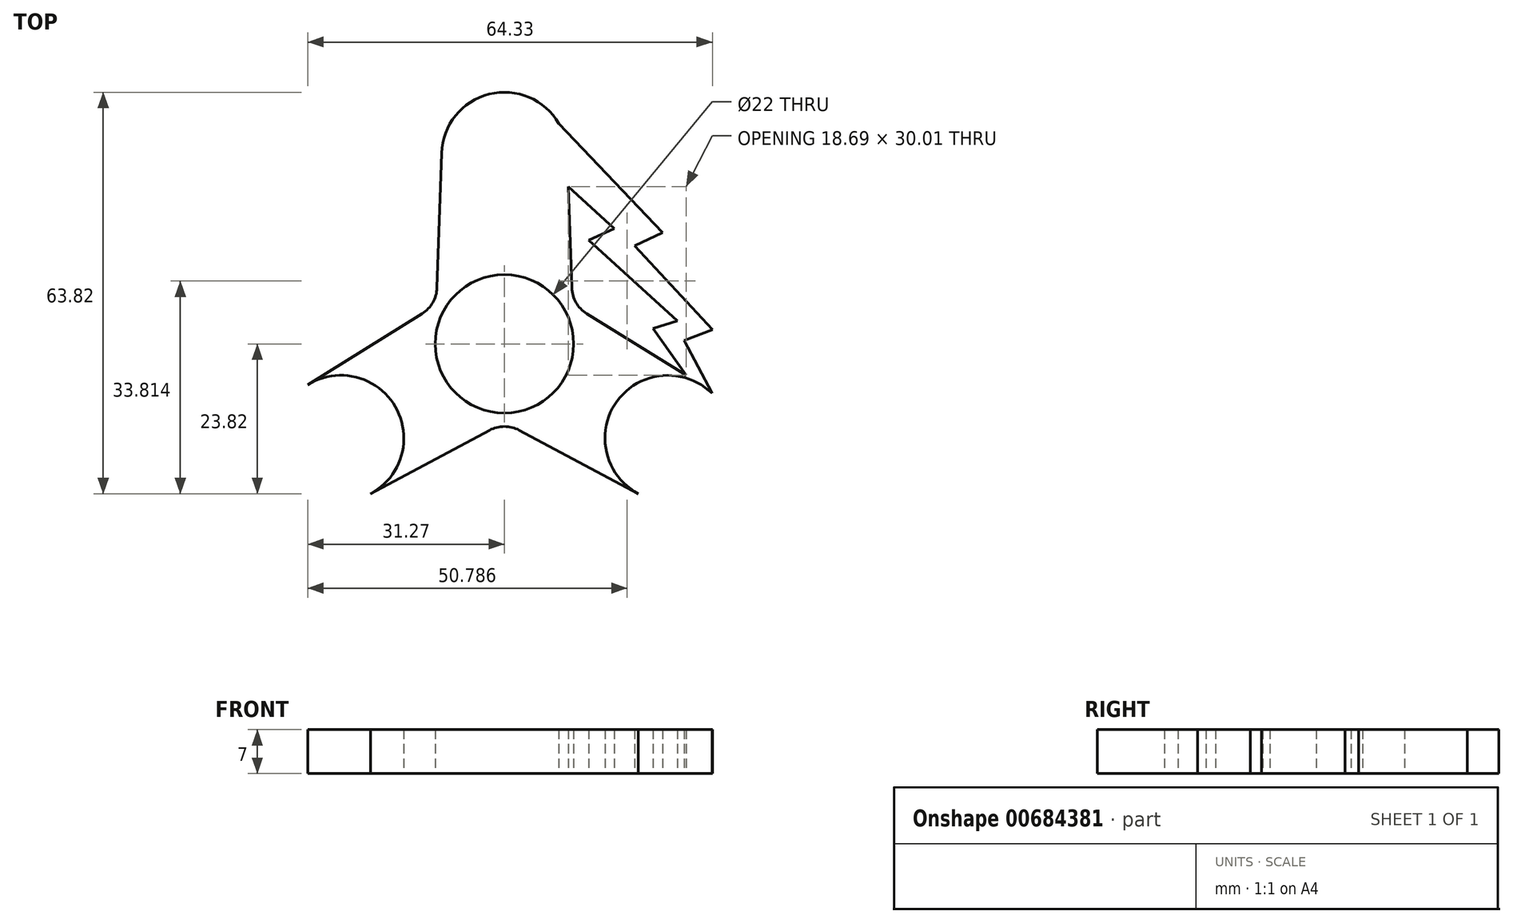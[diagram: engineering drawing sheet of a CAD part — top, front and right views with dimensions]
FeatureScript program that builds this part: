
annotation { "Feature Type Name" : "Feature", "Feature Type Description" : "" }
export const myFeature = defineFeature(function(context is Context, id is Id, definition is map)
    precondition{}
    {
        {
            var Q0;
            Q0=qCreatedBy(makeId("Top.planeOp"),FACE);
            var sketch = newSketch(context, id + "F0", { "sketchPlane" : qUnion([Q0])});
            skCircle(sketch, "E0", {"center": v(0, 0) * mm, "radius": 11 * mm});
            skLineSegment(sketch, "E1", {"start": v(-51.96, 30) * mm, "end": v(51.96, -30) * mm, "construction": true});
            skLineSegment(sketch, "E2.MirrorCS", {"start": v(51.96, 30) * mm, "end": v(-51.96, -30) * mm, "construction": true});
            skCircle(sketch, "E3", {"center": v(0, 30) * mm, "radius": 10 * mm});
            skCircle(sketch, "E4.MirrorC", {"center": v(-25.98, -15) * mm, "radius": 10 * mm});
            skCircle(sketch, "E5.MirrorC", {"center": v(25.98, -15) * mm, "radius": 10 * mm});
            skLineSegment(sketch, "E6", {"start": v(-10, 30.33) * mm, "end": v(-10.7, 8.9) * mm});
            skLineSegment(sketch, "E7", {"start": v(-13.06, 4.82) * mm, "end": v(-31.27, -6.51) * mm});
            skLineSegment(sketch, "E8", {"start": v(10, 30.33) * mm, "end": v(10.7, 8.9) * mm});
            skLineSegment(sketch, "E9.MirrorCS", {"start": v(-21.27, -23.82) * mm, "end": v(-2.35, -13.73) * mm});
            skLineSegment(sketch, "E10.MirrorCS", {"start": v(21.27, -23.82) * mm, "end": v(2.35, -13.73) * mm});
            skLineSegment(sketch, "E11.MirrorCS", {"start": v(31.27, -6.51) * mm, "end": v(13.06, 4.82) * mm});
            skPoint(sketch, "E12.newPointA", {"position": v(-11, 0) * mm});
            skArc(sketch, "E12.filletArc", {"start": v(-13.06, 4.82) * mm, "mid": v(-11.38, 6.57) * mm, "end": v(-10.7, 8.9) * mm});
            skPoint(sketch, "E13.newPointA", {"position": v(5.5, 9.53) * mm});
            skPoint(sketch, "E13.newPointB", {"position": v(11, 0) * mm});
            skArc(sketch, "E13.filletArc", {"start": v(10.7, 8.9) * mm, "mid": v(11.38, 6.57) * mm, "end": v(13.06, 4.82) * mm});
            skPoint(sketch, "E14.newPointA", {"position": v(5.5, -9.53) * mm});
            skPoint(sketch, "E14.newPointB", {"position": v(-5.5, -9.53) * mm});
            skArc(sketch, "E14.filletArc", {"start": v(2.35, -13.73) * mm, "mid": v(0, -13.14) * mm, "end": v(-2.35, -13.73) * mm});
            skLineSegment(sketch, "E15", {"start": v(-14.38, 35) * mm, "end": v(15.62, 35) * mm, "construction": true});
            skLineSegment(sketch, "E16", {"start": v(-14.38, 25) * mm, "end": v(15.62, 25) * mm, "construction": true});
            skLineSegment(sketch, "E17", {"start": v(12.92, -32.63) * mm, "end": v(38.07, 10.94) * mm, "construction": true});
            skLineSegment(sketch, "E18", {"start": v(17.47, -34.74) * mm, "end": v(42.44, 8.5) * mm, "construction": true});
            skLineSegment(sketch, "E19", {"start": v(10.17, 25) * mm, "end": v(17.47, 18.34) * mm});
            skLineSegment(sketch, "E20", {"start": v(8.66, 35) * mm, "end": v(25.12, 17.7) * mm});
            skLineSegment(sketch, "E21", {"start": v(17.47, 18.34) * mm, "end": v(13.41, 16.5) * mm});
            skLineSegment(sketch, "E22", {"start": v(13.41, 16.5) * mm, "end": v(27.48, 3.65) * mm});
            skLineSegment(sketch, "E23", {"start": v(27.48, 3.65) * mm, "end": v(23.63, 2.46) * mm});
            skLineSegment(sketch, "E24", {"start": v(23.63, 2.46) * mm, "end": v(28.86, -5.01) * mm});
            skLineSegment(sketch, "E25", {"start": v(25.12, 17.7) * mm, "end": v(20.7, 15.57) * mm});
            skLineSegment(sketch, "E26", {"start": v(20.7, 15.57) * mm, "end": v(33.06, 2.26) * mm});
            skLineSegment(sketch, "E27", {"start": v(33.06, 2.26) * mm, "end": v(28.56, 0.54) * mm});
            skLineSegment(sketch, "E28", {"start": v(28.56, 0.54) * mm, "end": v(32.99, -7.86) * mm});
            skSolve(sketch);
        }
        {
            var Q0;
            Q0=makeQuery(id+"F0.imprint","IMPRINT",FACE,{"disambiguationData":[TD([[makeQuery(id+"F0.imprint","IMPRINT",EDGE,{"derivedFrom":sQuery(id+"F0.wireOp",EDGE,"E0")}),-1.0]])]});
            var Q1;
            {var subQ0=sQuery(id+"F0.wireOp",EDGE,"E3");var subQ1=makeQuery(id+"F0.imprint","INTERSECT",VERTEX,{"derivedFrom":[subQ0,sQuery(id+"F0.wireOp",EDGE,"E8")]});Q1=makeQuery(id+"F0.imprint","IMPRINT",FACE,{"disambiguationData":[TD([[makeQuery(id+"F0.imprint","IMPRINT",EDGE,{"disambiguationData":[TD([[subQ1,-1.0]])],"derivedFrom":subQ0}),1.0]])]});}
            var Q2;
            {var subQ0=sQuery(id+"F0.wireOp",EDGE,"E4.MirrorC");var subQ1=makeQuery(id+"F0.imprint","INTERSECT",VERTEX,{"derivedFrom":[subQ0,sQuery(id+"F0.wireOp",EDGE,"E7")]});Q2=makeQuery(id+"F0.imprint","IMPRINT",FACE,{"disambiguationData":[TD([[makeQuery(id+"F0.imprint","IMPRINT",EDGE,{"disambiguationData":[TD([[subQ1,1.0]])],"derivedFrom":subQ0}),-1.0]])]});}
            var Q3;
            {var subQ0=sQuery(id+"F0.wireOp",EDGE,"E5.MirrorC");var subQ1=makeQuery(id+"F0.imprint","INTERSECT",VERTEX,{"derivedFrom":[subQ0,sQuery(id+"F0.wireOp",EDGE,"E11.MirrorCS")]});Q3=makeQuery(id+"F0.imprint","IMPRINT",FACE,{"disambiguationData":[TD([[makeQuery(id+"F0.imprint","IMPRINT",EDGE,{"disambiguationData":[TD([[subQ1,-1.0]])],"derivedFrom":subQ0}),-1.0]])]});}
            var Q4;
            {var subQ5=sQuery(id+"F0.wireOp",EDGE,"E19");Q4=makeQuery(id+"F0.imprint","IMPRINT",FACE,{"disambiguationData":[TD([[makeQuery(id+"F0.imprint","IMPRINT",EDGE,{"derivedFrom":subQ5}),1.0]])]});}
            extrude(context, id + "F1", {"entities" : qUnion([Q0, Q1, Q2, Q3, Q4]), "depth" : 7 * mm, "offsetDistance" : 25 * mm});
        }
    });
